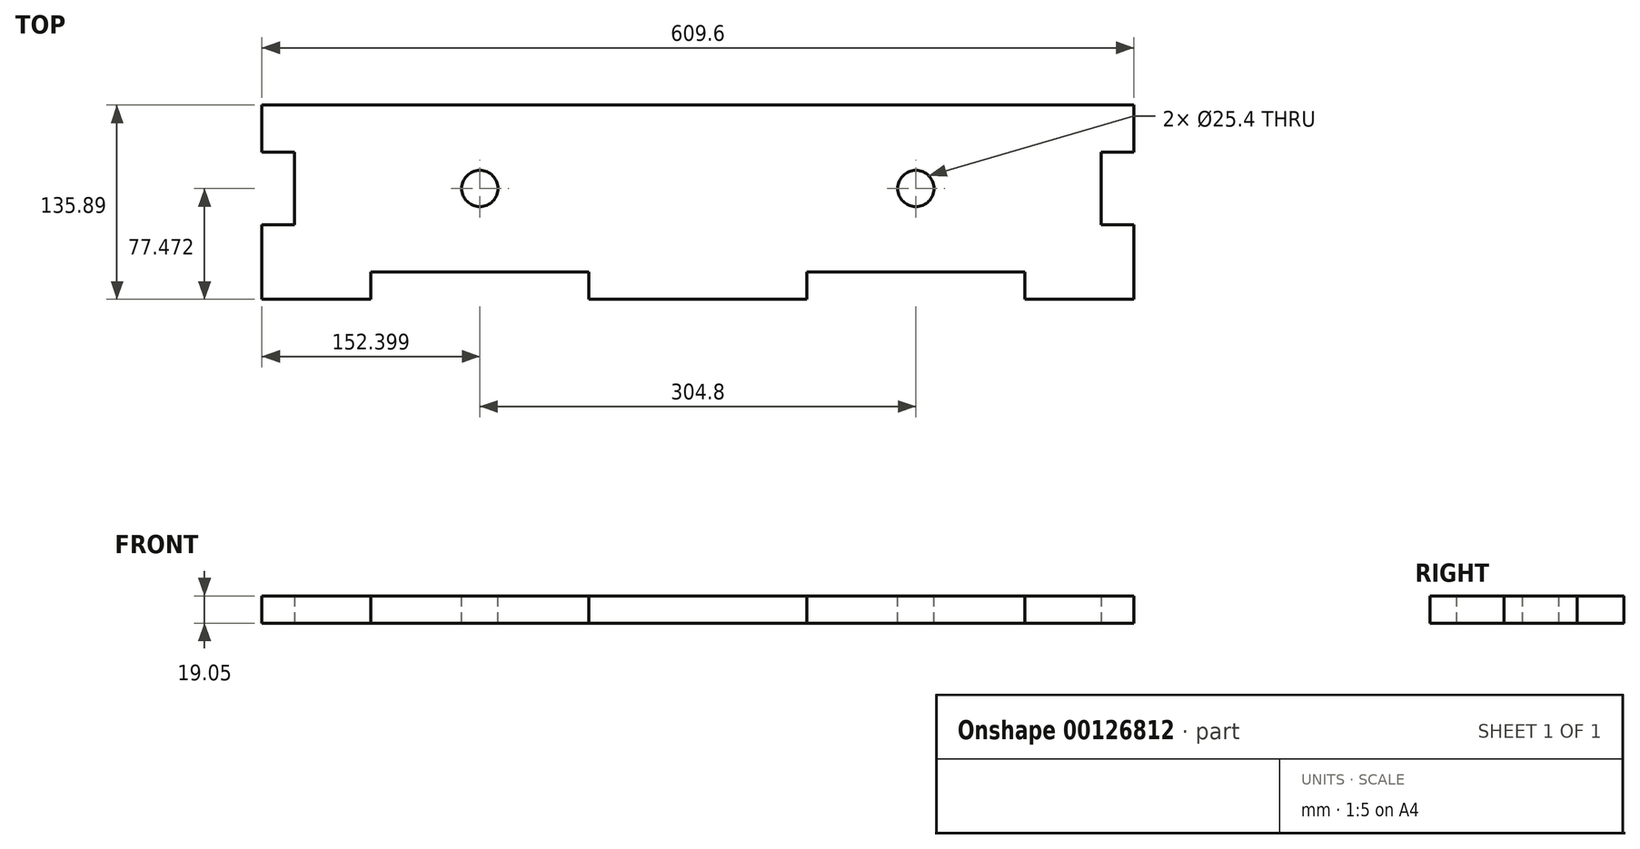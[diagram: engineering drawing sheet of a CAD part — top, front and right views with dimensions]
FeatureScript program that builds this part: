
annotation { "Feature Type Name" : "Feature", "Feature Type Description" : "" }
export const myFeature = defineFeature(function(context is Context, id is Id, definition is map)
    precondition{}
    {
        {
            var Q0;
            Q0=qCreatedBy(makeId("Top.planeOp"),FACE);
            var sketch = newSketch(context, id + "F0", { "sketchPlane" : qUnion([Q0])});
            skLineSegment(sketch, "E0.0", {"start": v(318.63, -53.72) * mm, "end": v(341.49, -53.72) * mm});
            skLineSegment(sketch, "E1.0", {"start": v(318.63, -2.92) * mm, "end": v(341.49, -2.92) * mm});
            skPoint(sketch, "E2.end.orphan", {"position": v(341.49, -28.32) * mm});
            skPoint(sketch, "E2.start.orphan", {"position": v(318.63, -10.03) * mm});
            skPoint(sketch, "E3.orphan", {"position": v(341.49, 30.1) * mm});
            skPoint(sketch, "E4.orphan", {"position": v(341.49, -86.74) * mm});
            skLineSegment(sketch, "E5.MirrorCS", {"start": v(-245.25, -2.92) * mm, "end": v(-268.11, -2.92) * mm});
            skLineSegment(sketch, "E6.MirrorCS", {"start": v(-245.25, -53.72) * mm, "end": v(-268.11, -53.72) * mm});
            skLineSegment(sketch, "E7", {"start": v(341.49, 30.1) * mm, "end": v(341.49, -2.92) * mm});
            skLineSegment(sketch, "E8", {"start": v(318.63, -2.92) * mm, "end": v(318.63, -53.72) * mm});
            skLineSegment(sketch, "E9.trimOffspring", {"start": v(341.49, -53.72) * mm, "end": v(341.49, -86.74) * mm});
            skLineSegment(sketch, "E10", {"start": v(-268.11, -53.72) * mm, "end": v(-268.11, -86.74) * mm});
            skLineSegment(sketch, "E11", {"start": v(-268.11, -2.92) * mm, "end": v(-268.11, 30.1) * mm});
            skLineSegment(sketch, "E12", {"start": v(-245.25, -2.92) * mm, "end": v(-245.25, -53.72) * mm});
            skPoint(sketch, "E13.bottom.start.orphan", {"position": v(-245.25, -86.74) * mm});
            skPoint(sketch, "E14.start.orphan", {"position": v(318.63, -80.13) * mm});
            skPoint(sketch, "E13.top.end.orphan", {"position": v(318.63, 60.07) * mm});
            skPoint(sketch, "E15.end.orphan", {"position": v(-245.25, 30.1) * mm});
            skLineSegment(sketch, "E16", {"start": v(-268.11, 30.1) * mm, "end": v(341.49, 30.1) * mm});
            skLineSegment(sketch, "E17", {"start": v(-245.25, -86.74) * mm, "end": v(-268.11, -86.74) * mm});
            skLineSegment(sketch, "E18.0", {"start": v(341.49, -105.79) * mm, "end": v(-268.11, -105.79) * mm});
            skLineSegment(sketch, "E19", {"start": v(341.49, -86.74) * mm, "end": v(341.49, -105.79) * mm});
            skLineSegment(sketch, "E20", {"start": v(-268.11, -86.74) * mm, "end": v(-268.11, -105.79) * mm});
            skSolve(sketch);
        }
        {
            var Q0;
            Q0 = qSketchRegion(id + "F0", true);
            extrude(context, id + "F1", {"entities" : qUnion([Q0]), "depth" : 19.05 * mm});
        }
        {
            var Q0;
            Q0=makeQuery(id+"F1.opExtrude","CAP_FACE",FACE,{"disambiguationData":[OSD([sQuery(id+"F0.wireOp",EDGE,"E0.0"),sQuery(id+"F0.wireOp",EDGE,"E1.0"),sQuery(id+"F0.wireOp",EDGE,"E5.MirrorCS"),sQuery(id+"F0.wireOp",EDGE,"E6.MirrorCS"),sQuery(id+"F0.wireOp",EDGE,"E7"),sQuery(id+"F0.wireOp",EDGE,"E8"),sQuery(id+"F0.wireOp",EDGE,"E9.trimOffspring"),sQuery(id+"F0.wireOp",EDGE,"E10"),sQuery(id+"F0.wireOp",EDGE,"E11"),sQuery(id+"F0.wireOp",EDGE,"E12"),sQuery(id+"F0.wireOp",EDGE,"E16"),sQuery(id+"F0.wireOp",EDGE,"E18.0"),sQuery(id+"F0.wireOp",EDGE,"E19"),sQuery(id+"F0.wireOp",EDGE,"E20")])],"isStart":false});
            var sketch = newSketch(context, id + "F2", { "sketchPlane" : qUnion([Q0])});
            skLineSegment(sketch, "E21", {"start": v(-268.11, -105.79) * mm, "end": v(-191.91, -105.79) * mm});
            skLineSegment(sketch, "E22.bottom", {"start": v(-191.91, -105.79) * mm, "end": v(-39.51, -105.79) * mm});
            skLineSegment(sketch, "E22.top", {"start": v(-191.91, -86.74) * mm, "end": v(-39.51, -86.74) * mm});
            skLineSegment(sketch, "E22.left", {"start": v(-191.91, -105.79) * mm, "end": v(-191.91, -86.74) * mm});
            skLineSegment(sketch, "E22.right", {"start": v(-39.51, -105.79) * mm, "end": v(-39.51, -86.74) * mm});
            skLineSegment(sketch, "E23.top", {"start": v(112.89, -86.74) * mm, "end": v(265.29, -86.74) * mm});
            skLineSegment(sketch, "E23.left", {"start": v(265.29, -105.79) * mm, "end": v(265.29, -86.74) * mm});
            skLineSegment(sketch, "E23.right", {"start": v(112.89, -105.79) * mm, "end": v(112.89, -86.74) * mm});
            skLineSegment(sketch, "E24", {"start": v(-39.51, -105.79) * mm, "end": v(112.89, -105.79) * mm});
            skLineSegment(sketch, "E25", {"start": v(112.89, -105.79) * mm, "end": v(265.29, -105.79) * mm});
            skSolve(sketch);
        }
        {
            var Q0;
            Q0 = qSketchRegion(id + "F2", true);
            extrude(context, id + "F3", {"entities" : qUnion([Q0]), "operationType" : NewBodyOperationType.REMOVE, "endBound" : BoundingType.THROUGH_ALL, "oppositeDirection" : true, "depth" : 25.4 * mm});
        }
        {
            var Q0;
            Q0=makeQuery(id+"F1.opExtrude","CAP_FACE",FACE,{"disambiguationData":[OSD([sQuery(id+"F0.wireOp",EDGE,"E0.0"),sQuery(id+"F0.wireOp",EDGE,"E1.0"),sQuery(id+"F0.wireOp",EDGE,"E5.MirrorCS"),sQuery(id+"F0.wireOp",EDGE,"E6.MirrorCS"),sQuery(id+"F0.wireOp",EDGE,"E7"),sQuery(id+"F0.wireOp",EDGE,"E8"),sQuery(id+"F0.wireOp",EDGE,"E9.trimOffspring"),sQuery(id+"F0.wireOp",EDGE,"E10"),sQuery(id+"F0.wireOp",EDGE,"E11"),sQuery(id+"F0.wireOp",EDGE,"E12"),sQuery(id+"F0.wireOp",EDGE,"E16"),sQuery(id+"F0.wireOp",EDGE,"E18.0"),sQuery(id+"F0.wireOp",EDGE,"E19"),sQuery(id+"F0.wireOp",EDGE,"E20")])],"isStart":false});
            var sketch = newSketch(context, id + "F4", { "sketchPlane" : qUnion([Q0])});
            skCircle(sketch, "E26", {"center": v(189.09, -28.32) * mm, "radius": 12.7 * mm});
            skCircle(sketch, "E27", {"center": v(-115.71, -28.32) * mm, "radius": 12.7 * mm});
            skSolve(sketch);
        }
        {
            var Q0;
            Q0 = qSketchRegion(id + "F4", true);
            extrude(context, id + "F5", {"entities" : qUnion([Q0]), "operationType" : NewBodyOperationType.REMOVE, "endBound" : BoundingType.THROUGH_ALL, "oppositeDirection" : true, "depth" : 25.4 * mm});
        }
    });
